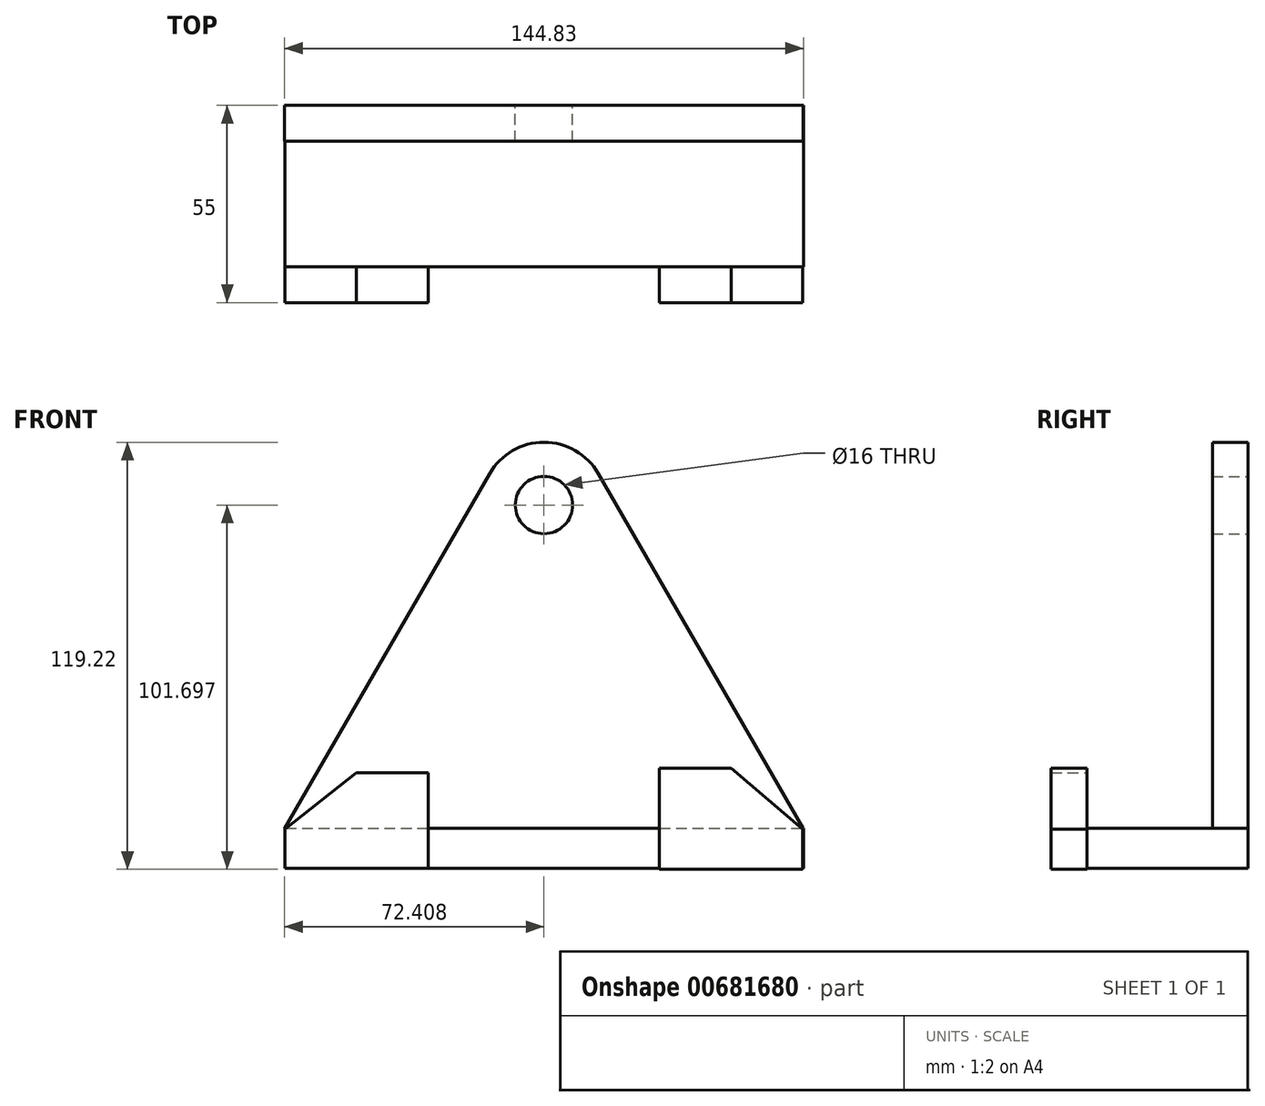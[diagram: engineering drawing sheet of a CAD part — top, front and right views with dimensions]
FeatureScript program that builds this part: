
annotation { "Feature Type Name" : "Feature", "Feature Type Description" : "" }
export const myFeature = defineFeature(function(context is Context, id is Id, definition is map)
    precondition{}
    {
        {
            var Q0;
            Q0=qCreatedBy(makeId("Front.planeOp"),FACE);
            var sketch = newSketch(context, id + "F0", { "sketchPlane" : qUnion([Q0])});
            skLineSegment(sketch, "E0.top", {"start": v(-71.33, -54.6) * mm, "end": v(73.48, -54.6) * mm});
            skLineSegment(sketch, "E1", {"start": v(-71.33, -54.6) * mm, "end": v(-14.1, 44.54) * mm});
            skLineSegment(sketch, "E2", {"start": v(16.25, 44.54) * mm, "end": v(73.48, -54.6) * mm});
            skArc(sketch, "E3", {"start": v(16.25, 44.54) * mm, "mid": v(1.08, 53.3) * mm, "end": v(-14.1, 44.54) * mm});
            skCircle(sketch, "E4", {"center": v(1.08, 35.78) * mm, "radius": 8 * mm});
            skSolve(sketch);
        }
        {
            var Q0;
            Q0=qCreatedBy(makeId("Front.planeOp"),FACE);
            var sketch = newSketch(context, id + "F1", { "sketchPlane" : qUnion([Q0])});
            skLineSegment(sketch, "E5.bottom", {"start": v(-71.25, -54.49) * mm, "end": v(73.5, -54.49) * mm});
            skLineSegment(sketch, "E5.left", {"start": v(-71.25, -54.49) * mm, "end": v(-71.25, -61.85) * mm});
            skLineSegment(sketch, "E5.right", {"start": v(73.5, -54.49) * mm, "end": v(73.5, -61.85) * mm});
            skLineSegment(sketch, "E6.top", {"start": v(-71.25, -65.68) * mm, "end": v(73.5, -65.68) * mm});
            skLineSegment(sketch, "E6.left", {"start": v(-71.25, -61.85) * mm, "end": v(-71.25, -65.68) * mm});
            skLineSegment(sketch, "E6.right", {"start": v(73.5, -61.85) * mm, "end": v(73.5, -65.68) * mm});
            skSolve(sketch);
        }
        {
            var Q0;
            Q0 = qSketchRegion(id + "F0", true);
            extrude(context, id + "F2", {"entities" : qUnion([Q0]), "depth" : 10 * mm, "offsetDistance" : 25 * mm});
        }
        {
            var Q0;
            Q0 = qSketchRegion(id + "F1", true);
            extrude(context, id + "F3", {"entities" : qUnion([Q0]), "operationType" : NewBodyOperationType.ADD, "depth" : 45 * mm, "offsetDistance" : 25 * mm});
        }
        {
            var Q0;
            Q0=makeQuery(id+"F3.opExtrude","CAP_FACE",FACE,{"disambiguationData":[OSD([sQuery(id+"F1.wireOp",EDGE,"E5.bottom"),sQuery(id+"F1.wireOp",EDGE,"E5.left"),sQuery(id+"F1.wireOp",EDGE,"E5.right"),sQuery(id+"F1.wireOp",EDGE,"E6.top"),sQuery(id+"F1.wireOp",EDGE,"E6.left"),sQuery(id+"F1.wireOp",EDGE,"E6.right")])],"isStart":false});
            var sketch = newSketch(context, id + "F4", { "sketchPlane" : qUnion([Q0])});
            skLineSegment(sketch, "E7.bottom", {"start": v(-71.25, -65.68) * mm, "end": v(-31.25, -65.68) * mm});
            skLineSegment(sketch, "E7.top", {"start": v(-51.25, -38.92) * mm, "end": v(-31.25, -38.92) * mm});
            skLineSegment(sketch, "E7.left", {"start": v(-71.25, -65.68) * mm, "end": v(-71.25, -54.64) * mm});
            skLineSegment(sketch, "E7.right", {"start": v(-31.25, -65.68) * mm, "end": v(-31.25, -38.92) * mm});
            skLineSegment(sketch, "E8.bottom", {"start": v(73.34, -65.92) * mm, "end": v(33.34, -65.92) * mm});
            skLineSegment(sketch, "E8.top", {"start": v(53.34, -37.73) * mm, "end": v(33.34, -37.73) * mm});
            skLineSegment(sketch, "E8.left", {"start": v(73.34, -65.92) * mm, "end": v(73.34, -54.64) * mm});
            skLineSegment(sketch, "E8.right", {"start": v(33.34, -65.92) * mm, "end": v(33.34, -37.73) * mm});
            skLineSegment(sketch, "E9", {"start": v(-71.25, -54.64) * mm, "end": v(-51.25, -38.92) * mm});
            skLineSegment(sketch, "E10", {"start": v(73.34, -54.64) * mm, "end": v(53.34, -37.73) * mm});
            skPoint(sketch, "E11.orphan", {"position": v(-71.25, -38.92) * mm});
            skPoint(sketch, "E12.orphan", {"position": v(73.34, -37.73) * mm});
            skSolve(sketch);
        }
        {
            var Q0;
            Q0 = qSketchRegion(id + "F4", true);
            extrude(context, id + "F5", {"entities" : qUnion([Q0]), "operationType" : NewBodyOperationType.ADD, "depth" : 10 * mm, "offsetDistance" : 25 * mm});
        }
    });
